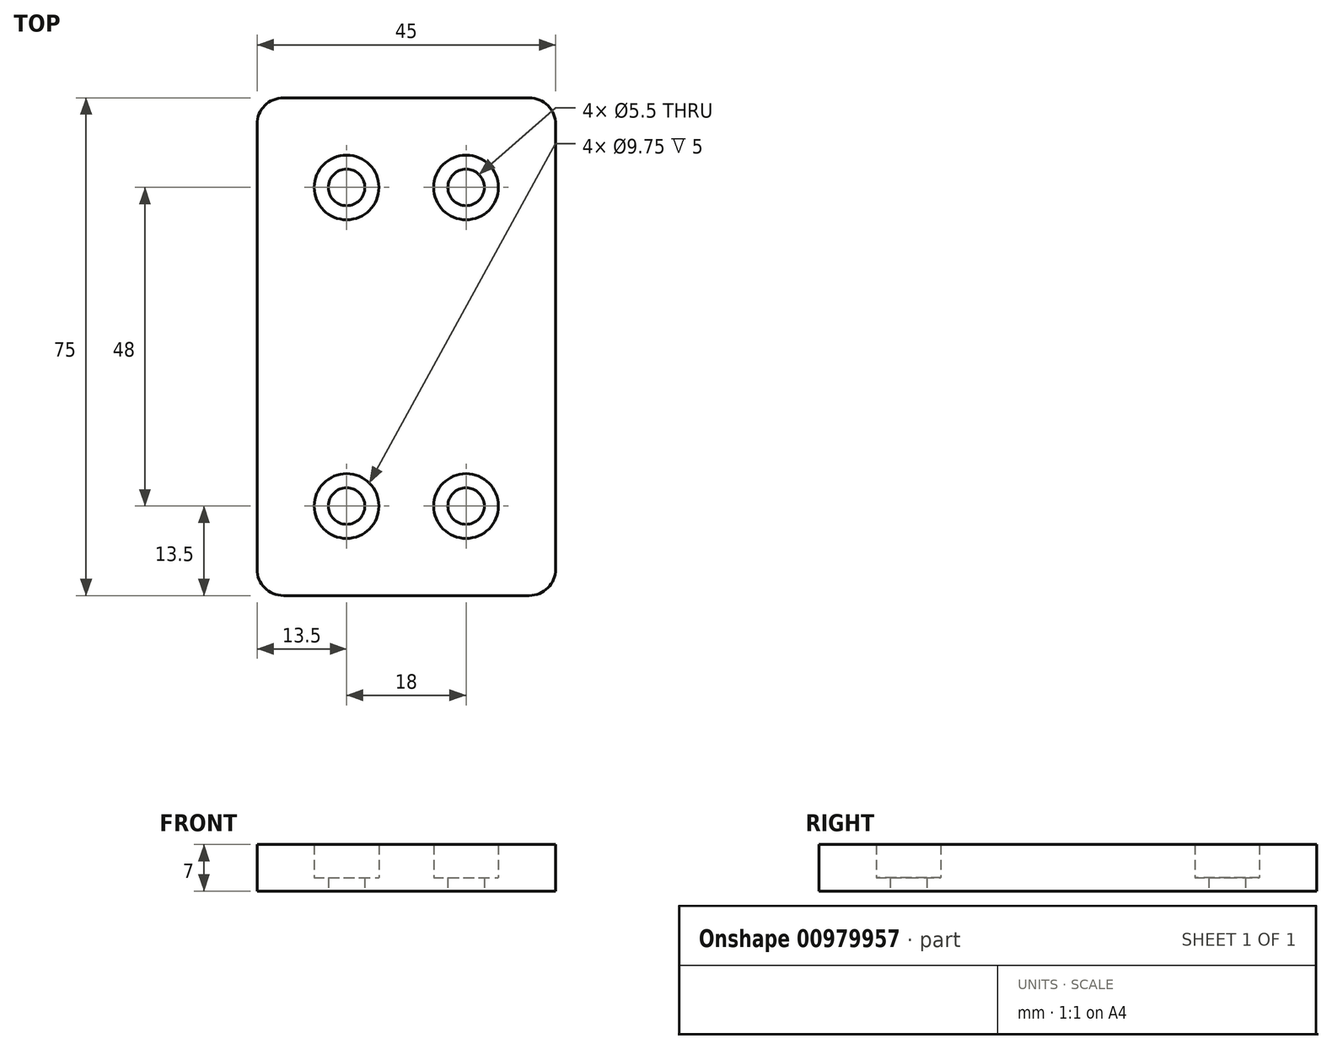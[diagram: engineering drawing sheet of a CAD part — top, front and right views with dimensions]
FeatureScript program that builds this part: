
annotation { "Feature Type Name" : "Feature", "Feature Type Description" : "" }
export const myFeature = defineFeature(function(context is Context, id is Id, definition is map)
    precondition{}
    {
        {
            var Q0;
            Q0=qCreatedBy(makeId("Top.planeOp"),FACE);
            var sketch = newSketch(context, id + "F0", { "sketchPlane" : qUnion([Q0])});
            skLineSegment(sketch, "E0.bottom", {"start": v(22.5, -37.5) * mm, "end": v(-22.5, -37.5) * mm});
            skLineSegment(sketch, "E0.top", {"start": v(22.5, 37.5) * mm, "end": v(-22.5, 37.5) * mm});
            skLineSegment(sketch, "E0.left", {"start": v(22.5, -37.5) * mm, "end": v(22.5, 37.5) * mm});
            skLineSegment(sketch, "E0.right", {"start": v(-22.5, -37.5) * mm, "end": v(-22.5, 37.5) * mm});
            skPoint(sketch, "E0.middle", {"position": v(0, 0) * mm});
            skSolve(sketch);
        }
        {
            var Q0;
            Q0 = qSketchRegion(id + "F0", true);
            extrude(context, id + "F1", {"entities" : qUnion([Q0]), "depth" : 7 * mm, "offsetDistance" : 25.4 * mm});
        }
        {
            var Q0;
            Q0=makeQuery(id+"F1.opExtrude","CAP_FACE",FACE,{"disambiguationData":[OSD([sQuery(id+"F0.wireOp",EDGE,"E0.bottom"),sQuery(id+"F0.wireOp",EDGE,"E0.top"),sQuery(id+"F0.wireOp",EDGE,"E0.left"),sQuery(id+"F0.wireOp",EDGE,"E0.right")])],"isStart":false});
            var sketch = newSketch(context, id + "F2", { "sketchPlane" : qUnion([Q0])});
            skPoint(sketch, "E1", {"position": v(-9, 24) * mm});
            skPoint(sketch, "E2", {"position": v(9, 24) * mm});
            skPoint(sketch, "E3", {"position": v(9, -24) * mm});
            skPoint(sketch, "E4", {"position": v(-9, -24) * mm});
            skSolve(sketch);
        }
        {
            var Q0;
            Q0=sQuery(id+"F2.wireOp",VERTEX,"E4");
            var Q1;
            Q1=sQuery(id+"F2.wireOp",VERTEX,"E3");
            var Q2;
            Q2=sQuery(id+"F2.wireOp",VERTEX,"E2");
            var Q3;
            Q3=sQuery(id+"F2.wireOp",VERTEX,"E1");
            var Q4;
            Q4=makeQuery(id+"F1.opExtrude","SWEPT_BODY",BODY,{"disambiguationData":[OSD([sQuery(id+"F0.wireOp",EDGE,"E0.bottom"),sQuery(id+"F0.wireOp",EDGE,"E0.top"),sQuery(id+"F0.wireOp",EDGE,"E0.left"),sQuery(id+"F0.wireOp",EDGE,"E0.right")])]});
            hole(context, id + "F3", {"style" : HoleStyle.C_BORE, "endStyle" : HoleEndStyle.THROUGH, "standardTappedOrClearance" : lookupTablePath({ "fit" : "Normal", "standard" : "ISO", "size" : "M5", "type" : "Clearance" }), "standardBlindInLast" : lookupTablePath({ "fit" : "Normal", "standard" : "ISO", "engagement" : "75%", "pitch" : "0.8 mm", "size" : "M5", "type" : "Clearance & tapped" }), "holeDiameter" : 5.5 * mm, "cBoreDiameter" : 9.75 * mm, "cBoreDepth" : 5 * mm, "majorDiameter" : 6.35 * mm, "isTappedThrough" : true, "tappedDepth" : 12.7 * mm, "tapClearance" : 3, "locations" : qUnion([Q0, Q1, Q2, Q3]), "scope" : qUnion([Q4]), "startStyle" : HoleStartStyle.PART});
        }
        {
            var Q0;
            Q0=makeQuery(id+"F1.opExtrude","SWEPT_EDGE",EDGE,{"disambiguationData":[OSD([sQuery(id+"F0.wireOp",EDGE,"E0.bottom"),sQuery(id+"F0.wireOp",EDGE,"E0.left")])]});
            var Q1;
            Q1=makeQuery(id+"F1.opExtrude","SWEPT_EDGE",EDGE,{"disambiguationData":[OSD([sQuery(id+"F0.wireOp",EDGE,"E0.bottom"),sQuery(id+"F0.wireOp",EDGE,"E0.right")])]});
            var Q2;
            Q2=makeQuery(id+"F1.opExtrude","SWEPT_EDGE",EDGE,{"disambiguationData":[OSD([sQuery(id+"F0.wireOp",EDGE,"E0.top"),sQuery(id+"F0.wireOp",EDGE,"E0.left")])]});
            var Q3;
            Q3=makeQuery(id+"F1.opExtrude","SWEPT_EDGE",EDGE,{"disambiguationData":[OSD([sQuery(id+"F0.wireOp",EDGE,"E0.top"),sQuery(id+"F0.wireOp",EDGE,"E0.right")])]});
            fillet(context, id + "F4", {"entities" : qUnion([Q0, Q1, Q2, Q3]), "radius" : 4 * mm, "tangentPropagation" : true, "allowEdgeOverflow" : false});
        }
    });
